# Revit family: Hager-VOLTA-Hollow_wall-Other-Without_Cover-Without_DIN-Hosted-PL-en
name_source: partatom
category: Electrical Equipment
units: mm (PartAtom-declared; Revit-internal decimal feet)

## family parameters
Cut with Voids When Loaded = No
Host = Face
Maintain Annotation Orientation = Yes
Panel Configuration = Two Columns, Circuits Across
Part Type = Panelboard
Room Calculation Point = No
Round Connector Dimension = Use Diameter
Shared = No

## types (5) — shared parameters
BC_MODEL_ID = 1547254
BC_OBJECT_ID = 513500
BC_OBJECT_VERSION = #5
Code hager = ADD-EC000214_EU
EF000003 - Mounting method = Hollow wall
EF000007 - Colour = White
EF000024 - UV resistant = No
EF000116 - RAL-number = 9010
EF000118 - With mounting plate = No
EF000218 - Built-in depth = 90 mm  [stored 0.295276 ft]
EF000846 - Built-in width = 314 mm  [stored 1.03018 ft]
EF001088 - Extension possible = Yes
EF001134 - DIN-rail = No
EF002950 - Width in number of modular spacings = 12
EF005474 - Degree of protection (IP) = Other
EF006244 - Transparent cover/door = No
EF006306 - With lock = No
EF015776 - Earthing terminal block = No
EF015777 - Neutral terminal block = No
EF015941 - Signal passing door = No
ETIM class code = EC000214
ETIM class name = Small distribution board
HG000002-With door or cover = No
HG000003-Range = VOLTA
HG000005-Thickness = 2 mm  [stored 0.00656168 ft]
HG000006-Flush mounted = Yes
HG000009-Double swing door = No
HG000010-Asymmetric doors = No
HG000011-Empty rows from bottom = No
HG000012-Door swing angle = 90.00°
HG000013-Door on the left = No
HG000014-Door on the right = Yes
HG000015-Clearance visibility = Yes
HG000016-Door 3D visibility = Yes
HG000017-Distance between poles = 18 mm  [stored 0.0590551 ft]
HG000060-RAL-number = 9010
HG000099-Onfly Template ID = 507532
HGEF002950-Width in number of modular spacings = 12
Manufacturer = Hager
Name = VOLTA-Hollow_wall-Other-Without_Cover-Without_DIN-PL
Name BIM&CO = Electricity
Name hager = ADD_Enclosures_EC000214
Uniformat = Low Tension Service & Dist.
Uniformat code = D501001
zero-valued in all types: Default Elevation, EF001131 - Inner depth, HG000001-Number of columns, HG000007-Number of empty columns, HG000008-Number of empty rows

## per-type parameters (varying)
| type | BC_VARIANT_ID | EF000008 - Width | EF000040 - Height | EF000049 - Depth | EF000266 - Number of rows | EF000332 - Built-in height | EF001062 - EMC-version | EF004462 - Type of closure | EF009212 - Cover model | HG000004-Manufacturer reference | HGEF000266-Number of rows |
| VOLTA-Hollow_wall_W330_H355_D94_12_Modular_Spacing-VH12NK | 1174398 | 330 mm | 355 mm | 94 mm  [stored 0.308399 ft] | 1 | 346 mm  [stored 1.13517 ft] | Yes |  | Closed | VH12NK | 1 |
| VOLTA-Hollow_wall_W348_H505_D98_12_Modular_Spacing-VH24NK | 1174399 | 348 mm  [stored 1.14173 ft] | 505 mm  [stored 1.65682 ft] | 98 mm  [stored 0.321522 ft] | 2 | 471 mm  [stored 1.54528 ft] | No | Other |  | VH24NK | 2 |
| VOLTA-Hollow_wall_W348_H630_D98_12_Modular_Spacing-VH36NK | 1174400 | 348 mm  [stored 1.14173 ft] | 630 mm  [stored 2.06693 ft] | 98 mm  [stored 0.321522 ft] | 3 | 596 mm  [stored 1.95538 ft] | No | Other |  | VH36NK | 3 |
| VOLTA-Hollow_wall_W348_H755_D98_12_Modular_Spacing-VH48NK | 1174401 | 348 mm  [stored 1.14173 ft] | 755 mm  [stored 2.47703 ft] | 98 mm  [stored 0.321522 ft] | 4 | 721 mm  [stored 2.36549 ft] | No | Other |  | VH48NK | 4 |
| VOLTA-Hollow_wall_W348_H880_D98_12_Modular_Spacing-VH60NK | 1174402 | 348 mm  [stored 1.14173 ft] | 880 mm  [stored 2.88714 ft] | 98 mm  [stored 0.321522 ft] | 5 | 846 mm  [stored 2.77559 ft] | No | Other |  | VH60NK | 5 |

note: column(s) folded — value = type name in every type: Reference

note: [stored X ft] marks values corroborated as IEEE doubles in the binary element streams (Revit-internal decimal feet)

## geometry (parser evidence)
native form markers: Sweep x14
no freeform markers — native parametric forms only
